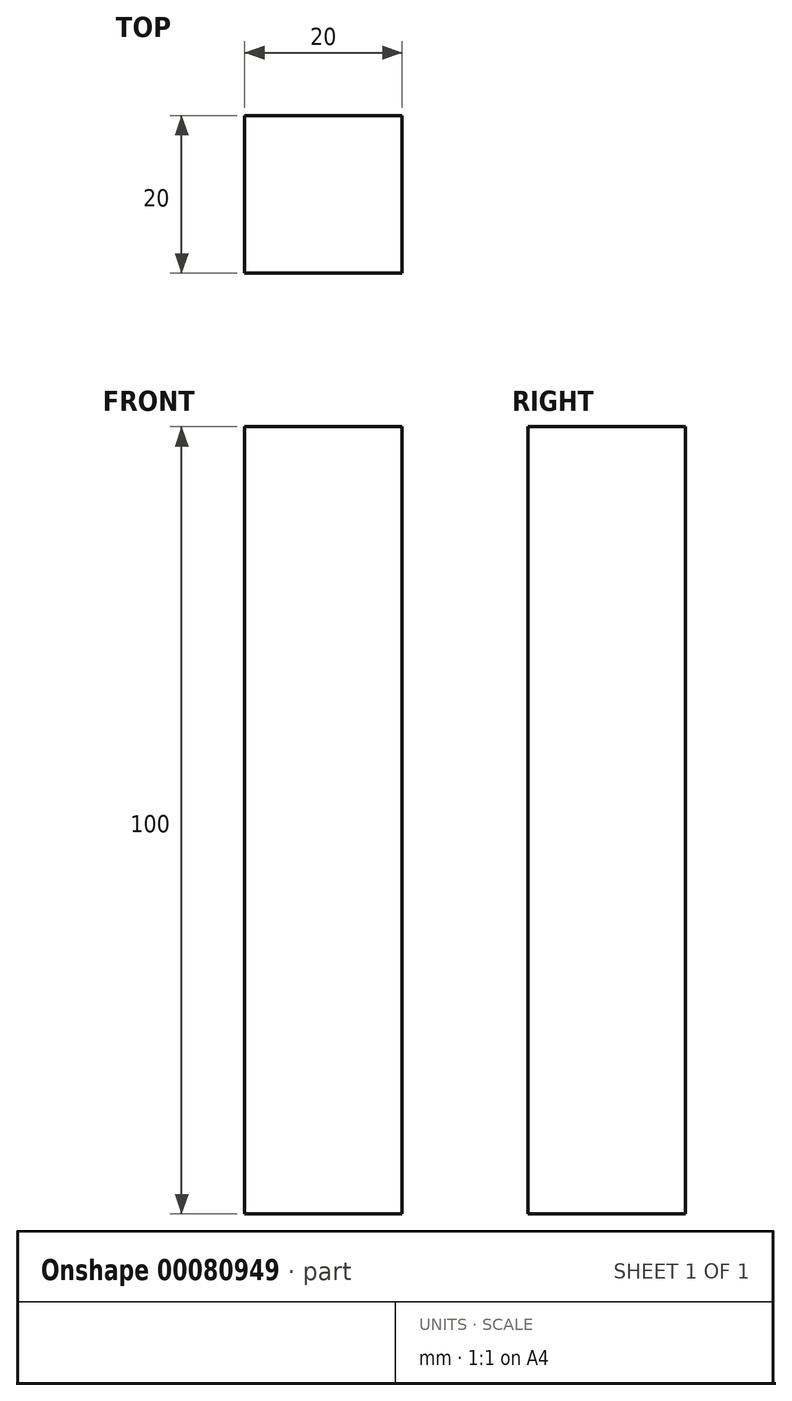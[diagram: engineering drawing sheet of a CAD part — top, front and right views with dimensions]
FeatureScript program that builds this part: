
annotation { "Feature Type Name" : "Feature", "Feature Type Description" : "" }
export const myFeature = defineFeature(function(context is Context, id is Id, definition is map)
    precondition{}
    {
        {
            var Q0;
            Q0=qCreatedBy(makeId("Top.planeOp"),FACE);
            var sketch = newSketch(context, id + "F0", { "sketchPlane" : qUnion([Q0])});
            skLineSegment(sketch, "E0.bottom", {"start": v(-26.51, 37.8) * mm, "end": v(-6.51, 37.8) * mm});
            skLineSegment(sketch, "E0.top", {"start": v(-26.51, 17.8) * mm, "end": v(-6.51, 17.8) * mm});
            skLineSegment(sketch, "E0.left", {"start": v(-26.51, 37.8) * mm, "end": v(-26.51, 17.8) * mm});
            skLineSegment(sketch, "E0.right", {"start": v(-6.51, 37.8) * mm, "end": v(-6.51, 17.8) * mm});
            skSolve(sketch);
        }
        {
            var Q0;
            Q0 = qSketchRegion(id + "F0", true);
            extrude(context, id + "F1", {"entities" : qUnion([Q0]), "offsetDistance" : 25 * mm, "depth" : 100 * mm});
        }
    });
